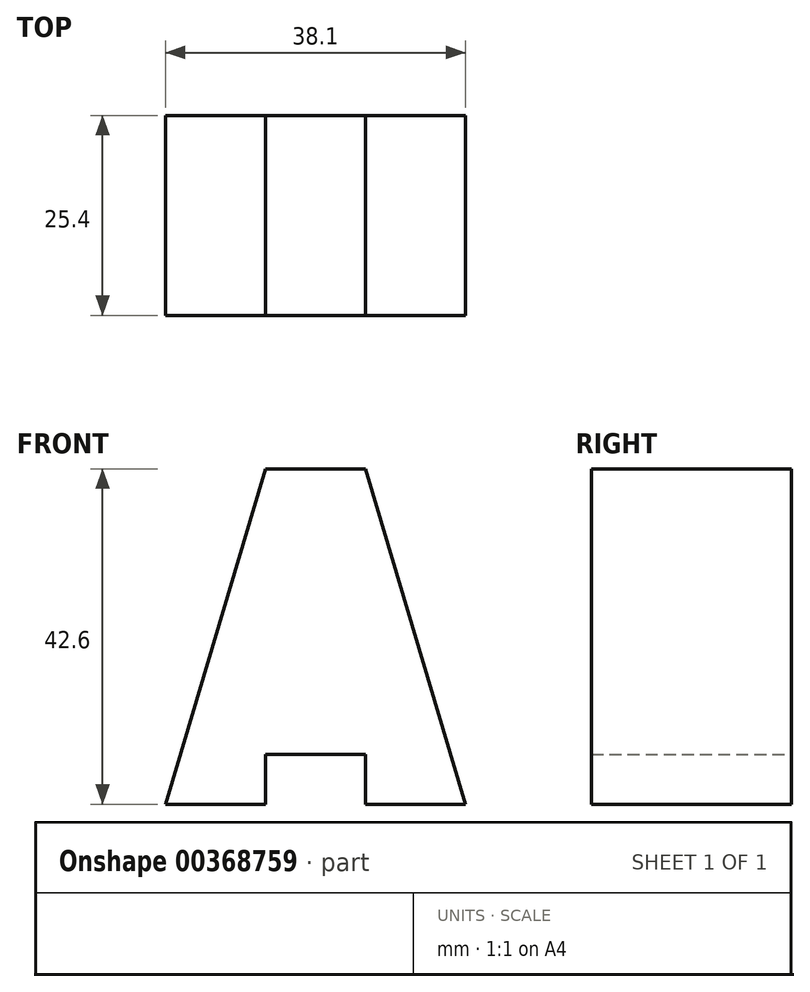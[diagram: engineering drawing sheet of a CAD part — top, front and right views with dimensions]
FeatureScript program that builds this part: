
annotation { "Feature Type Name" : "Feature", "Feature Type Description" : "" }
export const myFeature = defineFeature(function(context is Context, id is Id, definition is map)
    precondition{}
    {
        {
            var Q0;
            Q0=qCreatedBy(makeId("Front.planeOp"),FACE);
            var sketch = newSketch(context, id + "F0", { "sketchPlane" : qUnion([Q0])});
            skLineSegment(sketch, "E0", {"start": v(0, 0) * mm, "end": v(12.7, 0) * mm});
            skLineSegment(sketch, "E1", {"start": v(12.7, 0) * mm, "end": v(12.7, 6.35) * mm});
            skLineSegment(sketch, "E2", {"start": v(12.7, 6.35) * mm, "end": v(25.4, 6.35) * mm});
            skLineSegment(sketch, "E3", {"start": v(25.4, 6.35) * mm, "end": v(25.4, 0) * mm});
            skPoint(sketch, "E3.endSnap0", {"position": v(6.35, 0) * mm});
            skLineSegment(sketch, "E4", {"start": v(25.4, 0) * mm, "end": v(38.1, 0) * mm});
            skLineSegment(sketch, "E5", {"start": v(38.1, 0) * mm, "end": v(25.4, 42.6) * mm});
            skLineSegment(sketch, "E6", {"start": v(25.4, 42.6) * mm, "end": v(12.7, 42.6) * mm});
            skLineSegment(sketch, "E7", {"start": v(12.7, 42.6) * mm, "end": v(0, 0) * mm});
            skSolve(sketch);
        }
        {
            var Q0;
            Q0=qSketchRegion(id+"F0",true);
            extrude(context, id + "F1", {"entities" : qUnion([Q0]), "depth" : 25.4 * mm});
        }
    });
